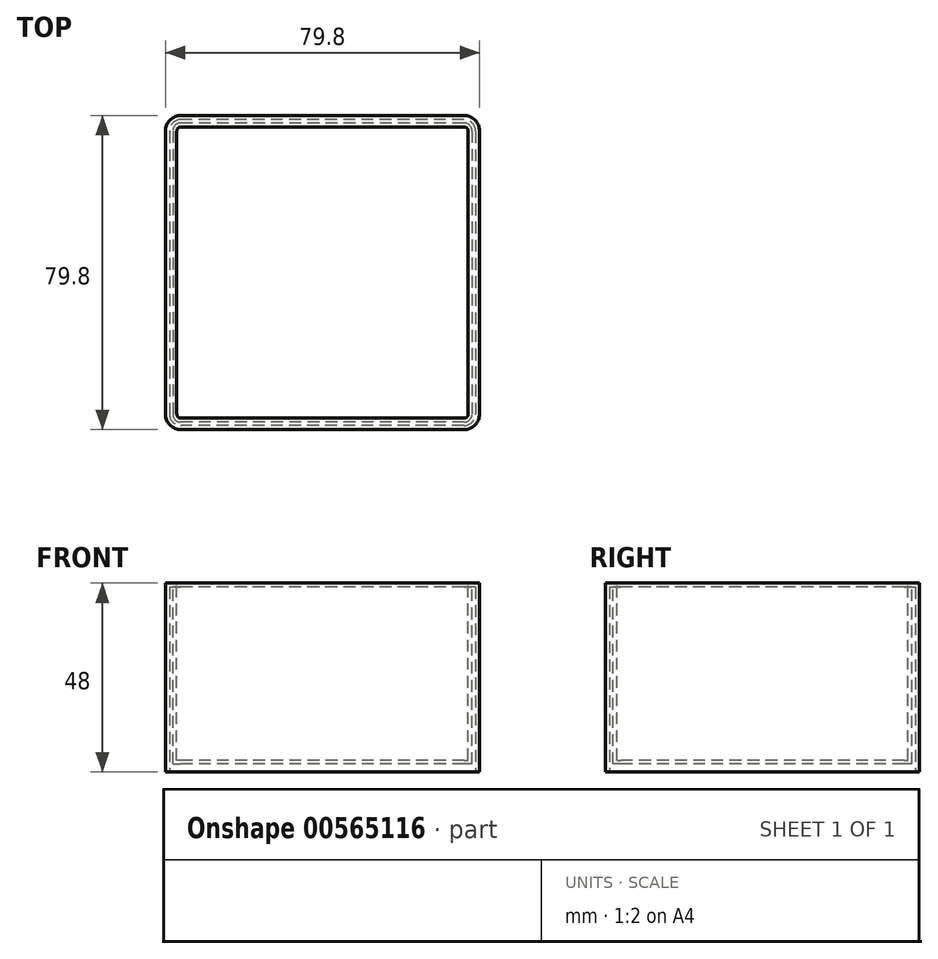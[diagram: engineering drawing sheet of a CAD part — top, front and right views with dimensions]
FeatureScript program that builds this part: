
annotation { "Feature Type Name" : "Feature", "Feature Type Description" : "" }
export const myFeature = defineFeature(function(context is Context, id is Id, definition is map)
    precondition{}
    {
        {
            var Q0;
            Q0=qCreatedBy(makeId("Top.planeOp"),FACE);
            var sketch = newSketch(context, id + "F0", { "sketchPlane" : qUnion([Q0])});
            skLineSegment(sketch, "E0.bottom", {"start": v(39.9, 39.9) * mm, "end": v(-39.9, 39.9) * mm});
            skLineSegment(sketch, "E0.top", {"start": v(39.9, -39.9) * mm, "end": v(-39.9, -39.9) * mm});
            skLineSegment(sketch, "E0.left", {"start": v(39.9, 39.9) * mm, "end": v(39.9, -39.9) * mm});
            skLineSegment(sketch, "E0.right", {"start": v(-39.9, 39.9) * mm, "end": v(-39.9, -39.9) * mm});
            skPoint(sketch, "E0.middle", {"position": v(0, 0) * mm});
            skSolve(sketch);
        }
        {
            var Q0;
            Q0 = qSketchRegion(id + "F0", true);
            extrude(context, id + "F1", {"entities" : qUnion([Q0]), "depth" : 48 * mm, "offsetDistance" : 25 * mm});
        }
        {
            var Q0;
            Q0=makeQuery(id+"F1.opExtrude","CAP_FACE",FACE,{"disambiguationData":[OSD([sQuery(id+"F0.wireOp",EDGE,"E0.bottom"),sQuery(id+"F0.wireOp",EDGE,"E0.top"),sQuery(id+"F0.wireOp",EDGE,"E0.left"),sQuery(id+"F0.wireOp",EDGE,"E0.right")])],"isStart":false});
            var sketch = newSketch(context, id + "F2", { "sketchPlane" : qUnion([Q0])});
            skLineSegment(sketch, "E1.bottom", {"start": v(37, 37) * mm, "end": v(-37, 37) * mm});
            skLineSegment(sketch, "E1.top", {"start": v(37, -37) * mm, "end": v(-37, -37) * mm});
            skLineSegment(sketch, "E1.left", {"start": v(37, 37) * mm, "end": v(37, -37) * mm});
            skLineSegment(sketch, "E1.right", {"start": v(-37, 37) * mm, "end": v(-37, -37) * mm});
            skPoint(sketch, "E1.middle", {"position": v(0, 0) * mm});
            skSolve(sketch);
        }
        {
            var Q0;
            Q0 = qSketchRegion(id + "F2", true);
            extrude(context, id + "F3", {"entities" : qUnion([Q0]), "operationType" : NewBodyOperationType.REMOVE, "oppositeDirection" : true, "depth" : 45 * mm, "offsetDistance" : 25 * mm});
        }
        {
            var Q0;
            Q0=makeQuery(id+"F1.opExtrude","SWEPT_EDGE",EDGE,{"disambiguationData":[OSD([sQuery(id+"F0.wireOp",EDGE,"E0.top"),sQuery(id+"F0.wireOp",EDGE,"E0.right")])]});
            var Q1;
            Q1=makeQuery(id+"F1.opExtrude","SWEPT_EDGE",EDGE,{"disambiguationData":[OSD([sQuery(id+"F0.wireOp",EDGE,"E0.top"),sQuery(id+"F0.wireOp",EDGE,"E0.left")])]});
            var Q2;
            Q2=makeQuery(id+"F1.opExtrude","SWEPT_EDGE",EDGE,{"disambiguationData":[OSD([sQuery(id+"F0.wireOp",EDGE,"E0.bottom"),sQuery(id+"F0.wireOp",EDGE,"E0.left")])]});
            var Q3;
            Q3=makeQuery(id+"F1.opExtrude","SWEPT_EDGE",EDGE,{"disambiguationData":[OSD([sQuery(id+"F0.wireOp",EDGE,"E0.bottom"),sQuery(id+"F0.wireOp",EDGE,"E0.right")])]});
            fillet(context, id + "F4", {"entities" : qUnion([Q0, Q1, Q2, Q3]), "radius" : 4 * mm, "tangentPropagation" : true, "allowEdgeOverflow" : false});
        }
        {
            var Q0;
            Q0=makeQuery(id+"F3.boolean.opBoolean","COPY",EDGE,{"derivedFrom":makeQuery(id+"F3.opExtrude","SWEPT_EDGE",EDGE,{"disambiguationData":[OSD([sQuery(id+"F2.wireOp",EDGE,"E1.top"),sQuery(id+"F2.wireOp",EDGE,"E1.right")])]})});
            var Q1;
            Q1=makeQuery(id+"F3.boolean.opBoolean","COPY",EDGE,{"derivedFrom":makeQuery(id+"F3.opExtrude","SWEPT_EDGE",EDGE,{"disambiguationData":[OSD([sQuery(id+"F2.wireOp",EDGE,"E1.bottom"),sQuery(id+"F2.wireOp",EDGE,"E1.right")])]})});
            var Q2;
            Q2=makeQuery(id+"F3.boolean.opBoolean","COPY",EDGE,{"derivedFrom":makeQuery(id+"F3.opExtrude","SWEPT_EDGE",EDGE,{"disambiguationData":[OSD([sQuery(id+"F2.wireOp",EDGE,"E1.bottom"),sQuery(id+"F2.wireOp",EDGE,"E1.left")])]})});
            var Q3;
            Q3=makeQuery(id+"F3.boolean.opBoolean","COPY",EDGE,{"derivedFrom":makeQuery(id+"F3.opExtrude","SWEPT_EDGE",EDGE,{"disambiguationData":[OSD([sQuery(id+"F2.wireOp",EDGE,"E1.top"),sQuery(id+"F2.wireOp",EDGE,"E1.left")])]})});
            fillet(context, id + "F5", {"entities" : qUnion([Q0, Q1, Q2, Q3]), "radius" : 1 * mm, "tangentPropagation" : true, "allowEdgeOverflow" : false});
        }
        {
            var Q0;
            Q0=makeQuery(id+"F1.opExtrude","CAP_FACE",FACE,{"disambiguationData":[OSD([sQuery(id+"F0.wireOp",EDGE,"E0.bottom"),sQuery(id+"F0.wireOp",EDGE,"E0.top"),sQuery(id+"F0.wireOp",EDGE,"E0.left"),sQuery(id+"F0.wireOp",EDGE,"E0.right")])],"isStart":true});
            shell(context, id + "F6", {"entities" : qUnion([Q0]), "thickness" : 1 * mm});
        }
    });
